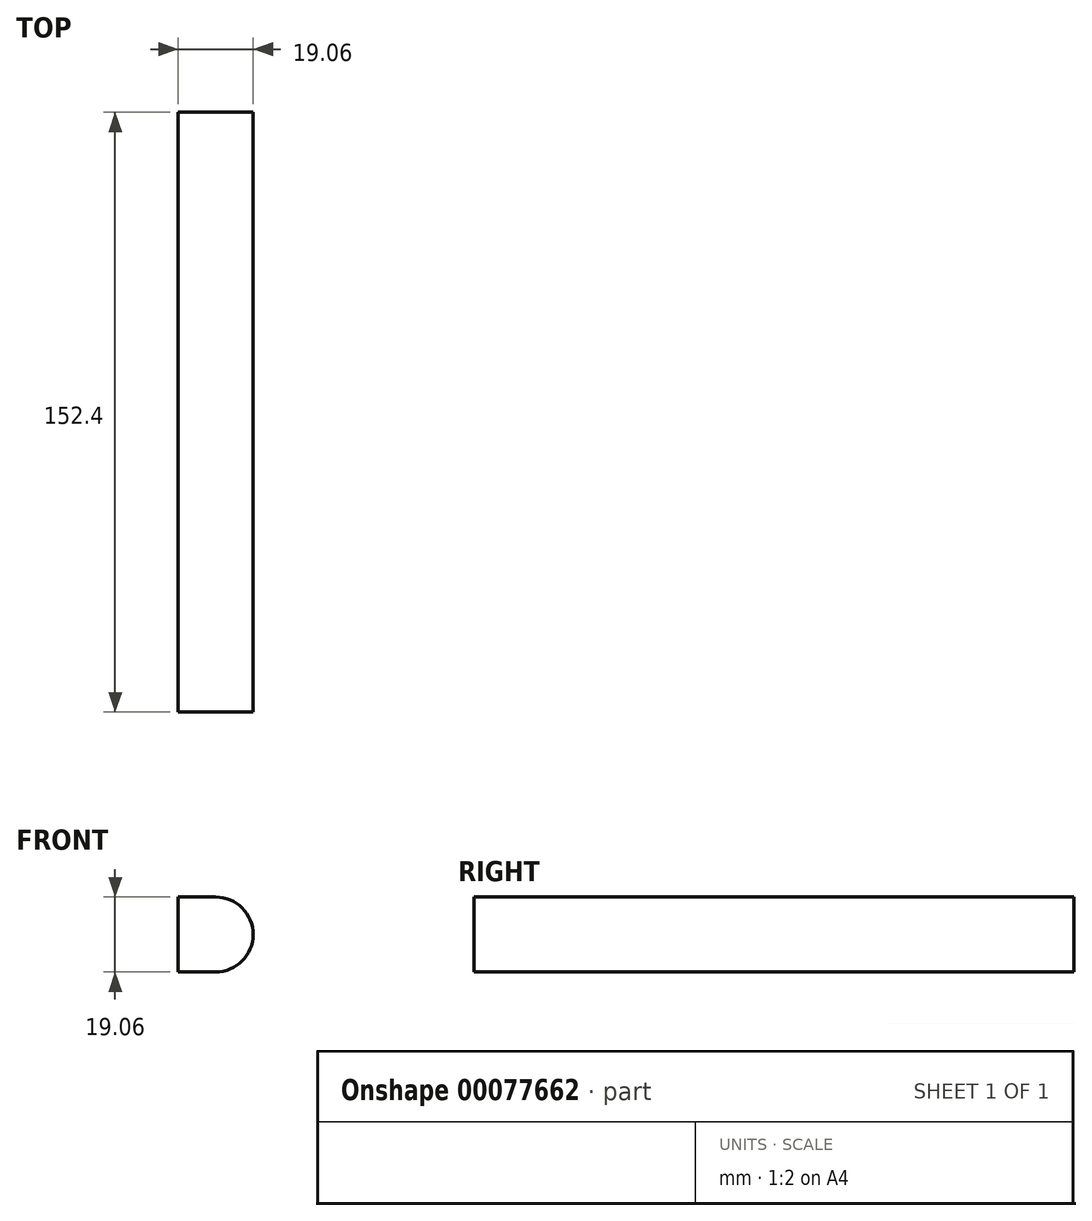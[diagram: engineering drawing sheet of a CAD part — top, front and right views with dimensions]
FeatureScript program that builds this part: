
annotation { "Feature Type Name" : "Feature", "Feature Type Description" : "" }
export const myFeature = defineFeature(function(context is Context, id is Id, definition is map)
    precondition{}
    {
        {
            var Q0;
            Q0=qCreatedBy(makeId("Front.planeOp"),FACE);
            var sketch = newSketch(context, id + "F0", { "sketchPlane" : qUnion([Q0])});
            skLineSegment(sketch, "E0", {"start": v(-9.53, 9.53) * mm, "end": v(0, 9.53) * mm});
            skLineSegment(sketch, "E1", {"start": v(0, -9.52) * mm, "end": v(-9.53, -9.52) * mm});
            skArc(sketch, "E2", {"start": v(9.53, 0) * mm, "mid": v(6.74, 6.74) * mm, "end": v(0, 9.53) * mm});
            skArc(sketch, "E3", {"start": v(0, -9.53) * mm, "mid": v(6.74, -6.74) * mm, "end": v(9.53, 0) * mm});
            skLineSegment(sketch, "E4", {"start": v(-9.53, -9.52) * mm, "end": v(-9.53, 9.52) * mm});
            skSolve(sketch);
        }
        {
            var Q0;
            Q0=makeQuery(id+"F0.imprint","IMPRINT",FACE,{"disambiguationData":[TD([[makeQuery(id+"F0.imprint","IMPRINT",EDGE,{"derivedFrom":sQuery(id+"F0.wireOp",EDGE,"E0")}),-1.0]])]});
            extrude(context, id + "F1", {"entities" : qUnion([Q0]), "depth" : 152.4 * mm});
        }
    });
